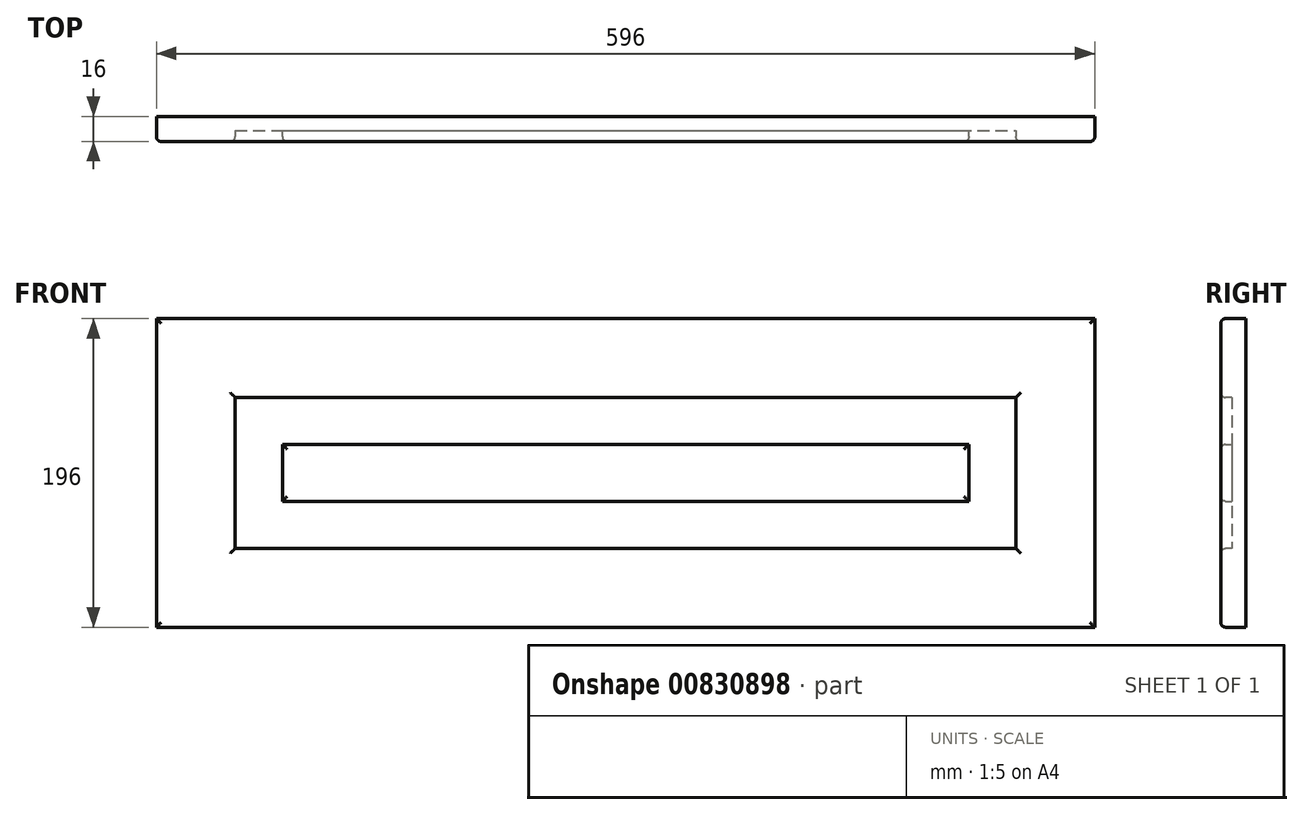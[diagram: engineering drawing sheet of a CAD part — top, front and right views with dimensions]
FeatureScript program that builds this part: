
annotation { "Feature Type Name" : "Feature", "Feature Type Description" : "" }
export const myFeature = defineFeature(function(context is Context, id is Id, definition is map)
    precondition{}
    {
        {
            var Q0;
            Q0=qCreatedBy(makeId("Front.planeOp"),FACE);
            var sketch = newSketch(context, id + "F0", { "sketchPlane" : qUnion([Q0])});
            skLineSegment(sketch, "E0.bottom", {"start": v(0, 0) * mm, "end": v(44.66, 0) * mm});
            skLineSegment(sketch, "E0.top", {"start": v(0, 33.8) * mm, "end": v(44.66, 33.8) * mm});
            skLineSegment(sketch, "E0.left", {"start": v(0, 0) * mm, "end": v(0, 33.8) * mm});
            skLineSegment(sketch, "E0.right", {"start": v(44.66, 0) * mm, "end": v(44.66, 33.8) * mm});
            skSolve(sketch);
        }
        {
            var Q0;
            Q0=makeQuery(id+"F0.imprint","IMPRINT",FACE,{"disambiguationData":[TD([[makeQuery(id+"F0.imprint","IMPRINT",EDGE,{"derivedFrom":sQuery(id+"F0.wireOp",EDGE,"E0.bottom")}),1.0]])]});
            extrude(context, id + "F1", {"entities" : qUnion([Q0]), "depth" : 16 * mm, "offsetDistance" : 25.4 * mm});
        }
        {
            var Q0;
            Q0=makeQuery(id+"F1.opExtrude","SWEPT_FACE",FACE,{"disambiguationData":[OSD([sQuery(id+"F0.wireOp",EDGE,"E0.bottom")])]});
            extrude(context, id + "F2", {"entities" : qUnion([Q0]), "operationType" : NewBodyOperationType.ADD, "oppositeDirection" : true, "depth" : 796 * mm, "offsetDistance" : 25 * mm});
        }
        {
            var Q0;
            {var subQ0=sQuery(id+"F0.wireOp",EDGE,"E0.left");Q0=makeQuery(id+"F2.boolean.opBoolean","MERGE",FACE,{"derivedFrom":[makeQuery(id+"F1.opExtrude","SWEPT_FACE",FACE,{"disambiguationData":[OSD([subQ0])]}),makeQuery(id+"F2.opExtrude","SWEPT_FACE",FACE,{"disambiguationData":[OSD([sQuery(id+"F0.wireOp",EDGE,"E0.bottom"),subQ0])]})]});}
            extrude(context, id + "F3", {"entities" : qUnion([Q0]), "operationType" : NewBodyOperationType.ADD, "oppositeDirection" : true, "depth" : 196 * mm, "offsetDistance" : 25 * mm});
        }
        {
            var Q0;
            {var subQ0=sQuery(id+"F0.wireOp",EDGE,"E0.left");var subQ1=sQuery(id+"F0.wireOp",EDGE,"E0.bottom");Q0=makeQuery(id+"F3.boolean.opBoolean","MERGE",FACE,{"derivedFrom":[makeQuery(id+"F2.boolean.opBoolean","MERGE",FACE,{"derivedFrom":[makeQuery(id+"F1.opExtrude","CAP_FACE",FACE,{"disambiguationData":[OSD([subQ1,sQuery(id+"F0.wireOp",EDGE,"E0.top"),subQ0,sQuery(id+"F0.wireOp",EDGE,"E0.right")])],"isStart":false}),makeQuery(id+"F2.opExtrude","SWEPT_FACE",FACE,{"disambiguationData":[OSD([subQ1]),TDD([makeQuery(id+"F1.opExtrude","CAP_EDGE",EDGE,{"disambiguationData":[OSD([subQ1])],"isStart":false})])]})]}),makeQuery(id+"F3.opExtrude","SWEPT_FACE",FACE,{"disambiguationData":[OSD([subQ1,subQ0]),TDD([makeQuery(id+"F2.boolean.opBoolean","MERGE",EDGE,{"derivedFrom":[makeQuery(id+"F1.opExtrude","CAP_EDGE",EDGE,{"disambiguationData":[OSD([subQ0])],"isStart":false}),makeQuery(id+"F2.opExtrude","SWEPT_EDGE",EDGE,{"disambiguationData":[OSD([subQ1,subQ0]),TDD([makeQuery(id+"F1.opExtrude","CAP_VERTEX",VERTEX,{"disambiguationData":[OSD([subQ1,subQ0])],"isStart":false})])]})]})])]})]});}
            var sketch = newSketch(context, id + "F4", { "sketchPlane" : qUnion([Q0])});
            skLineSegment(sketch, "E1.bottom", {"start": v(59.7, 646.67) * mm, "end": v(128.66, 646.67) * mm});
            skLineSegment(sketch, "E1.top", {"start": v(59.7, 152.97) * mm, "end": v(128.66, 152.97) * mm});
            skLineSegment(sketch, "E1.left", {"start": v(59.7, 646.67) * mm, "end": v(59.7, 152.97) * mm});
            skLineSegment(sketch, "E1.right", {"start": v(128.66, 646.67) * mm, "end": v(128.66, 152.97) * mm});
            skSolve(sketch);
        }
        {
            var Q0;
            Q0=makeQuery(id+"F4.imprint","IMPRINT",FACE,{"disambiguationData":[TD([[makeQuery(id+"F4.imprint","IMPRINT",EDGE,{"derivedFrom":sQuery(id+"F4.wireOp",EDGE,"E1.bottom")}),-1.0]])]});
            extrude(context, id + "F5", {"entities" : qUnion([Q0]), "operationType" : NewBodyOperationType.REMOVE, "oppositeDirection" : true, "depth" : 7 * mm, "offsetDistance" : 25 * mm});
        }
        {
            var Q0;
            Q0=makeQuery(id+"F5.boolean.opBoolean","COPY",FACE,{"derivedFrom":makeQuery(id+"F5.opExtrude","SWEPT_FACE",FACE,{"disambiguationData":[OSD([sQuery(id+"F4.wireOp",EDGE,"E1.left")])]})});
            extrude(context, id + "F6", {"entities" : qUnion([Q0]), "operationType" : NewBodyOperationType.REMOVE, "oppositeDirection" : true, "depth" : 9.7 * mm, "offsetDistance" : 25 * mm});
        }
        {
            var Q0;
            {var subQ0=sQuery(id+"F4.wireOp",EDGE,"E1.bottom");Q0=makeQuery(id+"F6.boolean.opBoolean","MERGE",FACE,{"derivedFrom":[makeQuery(id+"F5.boolean.opBoolean","COPY",FACE,{"derivedFrom":makeQuery(id+"F5.opExtrude","SWEPT_FACE",FACE,{"disambiguationData":[OSD([subQ0])]})}),makeQuery(id+"F6.opExtrude","SWEPT_FACE",FACE,{"disambiguationData":[OSD([subQ0,sQuery(id+"F4.wireOp",EDGE,"E1.left")])]})]});}
            extrude(context, id + "F7", {"entities" : qUnion([Q0]), "operationType" : NewBodyOperationType.ADD, "oppositeDirection" : true, "depth" : 99.33 * mm, "offsetDistance" : 25 * mm});
        }
        {
            var Q0;
            {var subQ0=sQuery(id+"F4.wireOp",EDGE,"E1.bottom");Q0=makeQuery(id+"F6.boolean.opBoolean","MERGE",FACE,{"derivedFrom":[makeQuery(id+"F5.boolean.opBoolean","COPY",FACE,{"derivedFrom":makeQuery(id+"F5.opExtrude","SWEPT_FACE",FACE,{"disambiguationData":[OSD([subQ0])]})}),makeQuery(id+"F6.opExtrude","SWEPT_FACE",FACE,{"disambiguationData":[OSD([subQ0,sQuery(id+"F4.wireOp",EDGE,"E1.left")])]})]});}
            extrude(context, id + "F8", {"entities" : qUnion([Q0]), "operationType" : NewBodyOperationType.REMOVE, "oppositeDirection" : true, "depth" : 99.33 * mm, "offsetDistance" : 25 * mm});
        }
        {
            var Q0;
            {var subQ0=sQuery(id+"F4.wireOp",EDGE,"E1.right");Q0=makeQuery(id+"F8.boolean.opBoolean","MERGE",FACE,{"derivedFrom":[makeQuery(id+"F5.boolean.opBoolean","COPY",FACE,{"derivedFrom":makeQuery(id+"F5.opExtrude","SWEPT_FACE",FACE,{"disambiguationData":[OSD([subQ0])]})}),makeQuery(id+"F8.opExtrude","SWEPT_FACE",FACE,{"disambiguationData":[OSD([sQuery(id+"F4.wireOp",EDGE,"E1.bottom"),subQ0])]})]});}
            extrude(context, id + "F9", {"entities" : qUnion([Q0]), "operationType" : NewBodyOperationType.REMOVE, "oppositeDirection" : true, "depth" : 17.34 * mm, "offsetDistance" : 25 * mm});
        }
        {
            var Q0;
            {var subQ0=sQuery(id+"F4.wireOp",EDGE,"E1.top");Q0=makeQuery(id+"F9.boolean.opBoolean","MERGE",FACE,{"derivedFrom":[makeQuery(id+"F6.boolean.opBoolean","MERGE",FACE,{"derivedFrom":[makeQuery(id+"F5.boolean.opBoolean","COPY",FACE,{"derivedFrom":makeQuery(id+"F5.opExtrude","SWEPT_FACE",FACE,{"disambiguationData":[OSD([subQ0])]})}),makeQuery(id+"F6.opExtrude","SWEPT_FACE",FACE,{"disambiguationData":[OSD([subQ0,sQuery(id+"F4.wireOp",EDGE,"E1.left")])]})]}),makeQuery(id+"F9.opExtrude","SWEPT_FACE",FACE,{"disambiguationData":[OSD([subQ0,sQuery(id+"F4.wireOp",EDGE,"E1.right")])]})]});}
            extrude(context, id + "F10", {"entities" : qUnion([Q0]), "operationType" : NewBodyOperationType.REMOVE, "oppositeDirection" : true, "depth" : 102.97 * mm, "offsetDistance" : 25 * mm});
        }
        {
            var Q0;
            {var subQ0=sQuery(id+"F4.wireOp",EDGE,"E1.right");var subQ1=sQuery(id+"F4.wireOp",EDGE,"E1.top");var subQ2=sQuery(id+"F4.wireOp",EDGE,"E1.left");var subQ3=sQuery(id+"F4.wireOp",EDGE,"E1.bottom");Q0=makeQuery(id+"F10.boolean.opBoolean","MERGE",FACE,{"derivedFrom":[makeQuery(id+"F9.boolean.opBoolean","MERGE",FACE,{"derivedFrom":[makeQuery(id+"F8.boolean.opBoolean","MERGE",FACE,{"derivedFrom":[makeQuery(id+"F6.boolean.opBoolean","MERGE",FACE,{"derivedFrom":[makeQuery(id+"F5.boolean.opBoolean","COPY",FACE,{"derivedFrom":makeQuery(id+"F5.opExtrude","CAP_FACE",FACE,{"disambiguationData":[OSD([subQ3,subQ1,subQ2,subQ0])],"isStart":false})}),makeQuery(id+"F6.opExtrude","SWEPT_FACE",FACE,{"disambiguationData":[OSD([subQ2]),TDD([makeQuery(id+"F5.boolean.opBoolean","COPY",EDGE,{"derivedFrom":makeQuery(id+"F5.opExtrude","CAP_EDGE",EDGE,{"disambiguationData":[OSD([subQ2])],"isStart":false})})])]})]}),makeQuery(id+"F8.opExtrude","SWEPT_FACE",FACE,{"disambiguationData":[OSD([subQ3,subQ2]),TDD([makeQuery(id+"F6.boolean.opBoolean","MERGE",EDGE,{"derivedFrom":[makeQuery(id+"F5.boolean.opBoolean","COPY",EDGE,{"derivedFrom":makeQuery(id+"F5.opExtrude","CAP_EDGE",EDGE,{"disambiguationData":[OSD([subQ3])],"isStart":false})}),makeQuery(id+"F6.opExtrude","SWEPT_EDGE",EDGE,{"disambiguationData":[OSD([subQ3,subQ2]),TDD([makeQuery(id+"F5.boolean.opBoolean","COPY",VERTEX,{"derivedFrom":makeQuery(id+"F5.opExtrude","CAP_VERTEX",VERTEX,{"disambiguationData":[OSD([subQ3,subQ2])],"isStart":false})})])]})]})])]})]}),makeQuery(id+"F9.opExtrude","SWEPT_FACE",FACE,{"disambiguationData":[OSD([subQ3,subQ0]),TDD([makeQuery(id+"F8.boolean.opBoolean","MERGE",EDGE,{"derivedFrom":[makeQuery(id+"F5.boolean.opBoolean","COPY",EDGE,{"derivedFrom":makeQuery(id+"F5.opExtrude","CAP_EDGE",EDGE,{"disambiguationData":[OSD([subQ0])],"isStart":false})}),makeQuery(id+"F8.opExtrude","SWEPT_EDGE",EDGE,{"disambiguationData":[OSD([subQ3,subQ0]),TDD([makeQuery(id+"F5.boolean.opBoolean","COPY",VERTEX,{"derivedFrom":makeQuery(id+"F5.opExtrude","CAP_VERTEX",VERTEX,{"disambiguationData":[OSD([subQ3,subQ0])],"isStart":false})})])]})]})])]})]}),makeQuery(id+"F10.opExtrude","SWEPT_FACE",FACE,{"disambiguationData":[OSD([subQ1,subQ2,subQ0]),TDD([makeQuery(id+"F9.boolean.opBoolean","MERGE",EDGE,{"derivedFrom":[makeQuery(id+"F6.boolean.opBoolean","MERGE",EDGE,{"derivedFrom":[makeQuery(id+"F5.boolean.opBoolean","COPY",EDGE,{"derivedFrom":makeQuery(id+"F5.opExtrude","CAP_EDGE",EDGE,{"disambiguationData":[OSD([subQ1])],"isStart":false})}),makeQuery(id+"F6.opExtrude","SWEPT_EDGE",EDGE,{"disambiguationData":[OSD([subQ1,subQ2]),TDD([makeQuery(id+"F5.boolean.opBoolean","COPY",VERTEX,{"derivedFrom":makeQuery(id+"F5.opExtrude","CAP_VERTEX",VERTEX,{"disambiguationData":[OSD([subQ1,subQ2])],"isStart":false})})])]})]}),makeQuery(id+"F9.opExtrude","SWEPT_EDGE",EDGE,{"disambiguationData":[OSD([subQ1,subQ0]),TDD([makeQuery(id+"F5.boolean.opBoolean","COPY",VERTEX,{"derivedFrom":makeQuery(id+"F5.opExtrude","CAP_VERTEX",VERTEX,{"disambiguationData":[OSD([subQ1,subQ0])],"isStart":false})})])]})]})])]})]});}
            var sketch = newSketch(context, id + "F11", { "sketchPlane" : qUnion([Q0])});
            skLineSegment(sketch, "E2.bottom", {"start": v(74.13, 678.73) * mm, "end": v(109.41, 678.73) * mm});
            skLineSegment(sketch, "E2.top", {"start": v(74.13, 186.63) * mm, "end": v(109.41, 186.63) * mm});
            skLineSegment(sketch, "E2.left", {"start": v(74.13, 678.73) * mm, "end": v(74.13, 186.63) * mm});
            skLineSegment(sketch, "E2.right", {"start": v(109.41, 678.73) * mm, "end": v(109.41, 186.63) * mm});
            skSolve(sketch);
        }
        {
            var Q0;
            Q0=makeQuery(id+"F11.imprint","IMPRINT",FACE,{"disambiguationData":[TD([[makeQuery(id+"F11.imprint","IMPRINT",EDGE,{"derivedFrom":sQuery(id+"F11.wireOp",EDGE,"E2.bottom")}),-1.0]])]});
            extrude(context, id + "F12", {"entities" : qUnion([Q0]), "operationType" : NewBodyOperationType.ADD, "depth" : 7 * mm, "offsetDistance" : 25 * mm});
        }
        {
            var Q0;
            Q0=makeQuery(id+"F12.opExtrude","SWEPT_FACE",FACE,{"disambiguationData":[OSD([sQuery(id+"F11.wireOp",EDGE,"E2.bottom")])]});
            extrude(context, id + "F13", {"entities" : qUnion([Q0]), "operationType" : NewBodyOperationType.ADD, "depth" : 37.27 * mm, "offsetDistance" : 25 * mm});
        }
        {
            var Q0;
            {var subQ0=sQuery(id+"F11.wireOp",EDGE,"E2.right");Q0=makeQuery(id+"F13.boolean.opBoolean","MERGE",FACE,{"derivedFrom":[makeQuery(id+"F12.opExtrude","SWEPT_FACE",FACE,{"disambiguationData":[OSD([subQ0])]}),makeQuery(id+"F13.opExtrude","SWEPT_FACE",FACE,{"disambiguationData":[OSD([sQuery(id+"F11.wireOp",EDGE,"E2.bottom"),subQ0])]})]});}
            extrude(context, id + "F14", {"entities" : qUnion([Q0]), "operationType" : NewBodyOperationType.ADD, "depth" : 6.58 * mm, "offsetDistance" : 25 * mm});
        }
        {
            var Q0;
            {var subQ0=sQuery(id+"F11.wireOp",EDGE,"E2.top");Q0=makeQuery(id+"F14.boolean.opBoolean","MERGE",FACE,{"derivedFrom":[makeQuery(id+"F12.opExtrude","SWEPT_FACE",FACE,{"disambiguationData":[OSD([subQ0])]}),makeQuery(id+"F14.opExtrude","SWEPT_FACE",FACE,{"disambiguationData":[OSD([subQ0,sQuery(id+"F11.wireOp",EDGE,"E2.right")])]})]});}
            extrude(context, id + "F15", {"entities" : qUnion([Q0]), "operationType" : NewBodyOperationType.ADD, "depth" : 106.63 * mm, "offsetDistance" : 25 * mm});
        }
        {
            var Q0;
            {var subQ0=sQuery(id+"F11.wireOp",EDGE,"E2.left");Q0=makeQuery(id+"F15.boolean.opBoolean","MERGE",FACE,{"derivedFrom":[makeQuery(id+"F13.boolean.opBoolean","MERGE",FACE,{"derivedFrom":[makeQuery(id+"F12.opExtrude","SWEPT_FACE",FACE,{"disambiguationData":[OSD([subQ0])]}),makeQuery(id+"F13.opExtrude","SWEPT_FACE",FACE,{"disambiguationData":[OSD([sQuery(id+"F11.wireOp",EDGE,"E2.bottom"),subQ0])]})]}),makeQuery(id+"F15.opExtrude","SWEPT_FACE",FACE,{"disambiguationData":[OSD([sQuery(id+"F11.wireOp",EDGE,"E2.top"),subQ0])]})]});}
            extrude(context, id + "F16", {"entities" : qUnion([Q0]), "operationType" : NewBodyOperationType.REMOVE, "oppositeDirection" : true, "depth" : 5.87 * mm, "offsetDistance" : 25 * mm});
        }
        {
            var Q0;
            Q0=makeQuery(id+"F3.opExtrude","CAP_FACE",FACE,{"disambiguationData":[OSD([sQuery(id+"F0.wireOp",EDGE,"E0.bottom"),sQuery(id+"F0.wireOp",EDGE,"E0.left")])],"isStart":false});
            extrude(context, id + "F17", {"entities" : qUnion([Q0]), "operationType" : NewBodyOperationType.ADD, "depth" : 200 * mm, "offsetDistance" : 25 * mm});
        }
        {
            var Q0;
            {var subQ0=sQuery(id+"F4.wireOp",EDGE,"E1.right");Q0=makeQuery(id+"F10.boolean.opBoolean","MERGE",FACE,{"derivedFrom":[makeQuery(id+"F9.boolean.opBoolean","COPY",FACE,{"derivedFrom":makeQuery(id+"F9.opExtrude","CAP_FACE",FACE,{"disambiguationData":[OSD([sQuery(id+"F4.wireOp",EDGE,"E1.bottom"),subQ0])],"isStart":false})}),makeQuery(id+"F10.opExtrude","SWEPT_FACE",FACE,{"disambiguationData":[OSD([sQuery(id+"F4.wireOp",EDGE,"E1.top"),subQ0])]})]});}
            extrude(context, id + "F18", {"entities" : qUnion([Q0]), "operationType" : NewBodyOperationType.REMOVE, "oppositeDirection" : true, "depth" : 200 * mm, "offsetDistance" : 25 * mm});
        }
        {
            var Q0;
            {var subQ0=sQuery(id+"F11.wireOp",EDGE,"E2.right");var subQ1=sQuery(id+"F11.wireOp",EDGE,"E2.top");Q0=makeQuery(id+"F15.boolean.opBoolean","MERGE",FACE,{"derivedFrom":[makeQuery(id+"F14.opExtrude","CAP_FACE",FACE,{"disambiguationData":[OSD([sQuery(id+"F11.wireOp",EDGE,"E2.bottom"),subQ0])],"isStart":false}),makeQuery(id+"F15.opExtrude","SWEPT_FACE",FACE,{"disambiguationData":[OSD([subQ1,subQ0]),TDD([makeQuery(id+"F14.opExtrude","CAP_EDGE",EDGE,{"disambiguationData":[OSD([subQ1,subQ0])],"isStart":false})])]})]});}
            extrude(context, id + "F19", {"entities" : qUnion([Q0]), "operationType" : NewBodyOperationType.ADD, "depth" : 200 * mm, "offsetDistance" : 25 * mm});
        }
        {
            var Q0;
            Q0=makeQuery(id+"F17.opExtrude","CAP_FACE",FACE,{"disambiguationData":[OSD([sQuery(id+"F0.wireOp",EDGE,"E0.bottom"),sQuery(id+"F0.wireOp",EDGE,"E0.left")])],"isStart":false});
            extrude(context, id + "F20", {"entities" : qUnion([Q0]), "operationType" : NewBodyOperationType.ADD, "depth" : 200 * mm, "offsetDistance" : 25 * mm});
        }
        {
            var Q0;
            Q0=makeQuery(id+"F18.boolean.opBoolean","COPY",FACE,{"derivedFrom":makeQuery(id+"F18.opExtrude","CAP_FACE",FACE,{"disambiguationData":[OSD([sQuery(id+"F4.wireOp",EDGE,"E1.bottom"),sQuery(id+"F4.wireOp",EDGE,"E1.top"),sQuery(id+"F4.wireOp",EDGE,"E1.right")])],"isStart":false})});
            extrude(context, id + "F21", {"entities" : qUnion([Q0]), "operationType" : NewBodyOperationType.REMOVE, "oppositeDirection" : true, "depth" : 200 * mm, "offsetDistance" : 25 * mm});
        }
        {
            var Q0;
            Q0=makeQuery(id+"F19.opExtrude","CAP_FACE",FACE,{"disambiguationData":[OSD([sQuery(id+"F11.wireOp",EDGE,"E2.bottom"),sQuery(id+"F11.wireOp",EDGE,"E2.top"),sQuery(id+"F11.wireOp",EDGE,"E2.right")])],"isStart":false});
            extrude(context, id + "F22", {"entities" : qUnion([Q0]), "operationType" : NewBodyOperationType.ADD, "depth" : 200 * mm, "offsetDistance" : 25 * mm});
        }
        {
            var Q0;
            {var subQ0=sQuery(id+"F11.wireOp",EDGE,"E2.right");var subQ1=sQuery(id+"F11.wireOp",EDGE,"E2.top");Q0=makeQuery(id+"F22.boolean.opBoolean","MERGE",FACE,{"derivedFrom":[makeQuery(id+"F19.boolean.opBoolean","MERGE",FACE,{"derivedFrom":[makeQuery(id+"F15.opExtrude","CAP_FACE",FACE,{"disambiguationData":[OSD([subQ1,subQ0])],"isStart":false}),makeQuery(id+"F19.opExtrude","SWEPT_FACE",FACE,{"disambiguationData":[OSD([subQ1,subQ0])]})]}),makeQuery(id+"F22.opExtrude","SWEPT_FACE",FACE,{"disambiguationData":[OSD([subQ1,subQ0])]})]});}
            extrude(context, id + "F23", {"entities" : qUnion([Q0]), "operationType" : NewBodyOperationType.REMOVE, "oppositeDirection" : true, "depth" : 600 * mm, "offsetDistance" : 25 * mm});
        }
        {
            var Q0;
            {var subQ0=sQuery(id+"F4.wireOp",EDGE,"E1.right");var subQ1=sQuery(id+"F4.wireOp",EDGE,"E1.top");Q0=makeQuery(id+"F21.boolean.opBoolean","MERGE",FACE,{"derivedFrom":[makeQuery(id+"F18.boolean.opBoolean","MERGE",FACE,{"derivedFrom":[makeQuery(id+"F10.boolean.opBoolean","COPY",FACE,{"derivedFrom":makeQuery(id+"F10.opExtrude","CAP_FACE",FACE,{"disambiguationData":[OSD([subQ1,sQuery(id+"F4.wireOp",EDGE,"E1.left"),subQ0])],"isStart":false})}),makeQuery(id+"F18.opExtrude","SWEPT_FACE",FACE,{"disambiguationData":[OSD([subQ1,subQ0])]})]}),makeQuery(id+"F21.opExtrude","SWEPT_FACE",FACE,{"disambiguationData":[OSD([subQ1,subQ0])]})]});}
            extrude(context, id + "F24", {"entities" : qUnion([Q0]), "operationType" : NewBodyOperationType.ADD, "depth" : 600 * mm, "offsetDistance" : 25 * mm});
        }
        {
            var Q0;
            {var subQ0=sQuery(id+"F0.wireOp",EDGE,"E0.left");var subQ1=sQuery(id+"F0.wireOp",EDGE,"E0.bottom");var subQ2=makeQuery(id+"F1.opExtrude","SWEPT_EDGE",EDGE,{"disambiguationData":[OSD([subQ1,subQ0])]});var subQ3=makeQuery(id+"F3.opExtrude","CAP_EDGE",EDGE,{"disambiguationData":[OSD([subQ1,subQ0]),TDD([subQ2])],"isStart":false});Q0=makeQuery(id+"F20.boolean.opBoolean","MERGE",FACE,{"derivedFrom":[makeQuery(id+"F17.boolean.opBoolean","MERGE",FACE,{"derivedFrom":[makeQuery(id+"F3.boolean.opBoolean","MERGE",FACE,{"derivedFrom":[makeQuery(id+"F1.opExtrude","SWEPT_FACE",FACE,{"disambiguationData":[OSD([subQ1])]}),makeQuery(id+"F3.opExtrude","SWEPT_FACE",FACE,{"disambiguationData":[OSD([subQ1,subQ0]),TDD([subQ2])]})]}),makeQuery(id+"F17.opExtrude","SWEPT_FACE",FACE,{"disambiguationData":[OSD([subQ1,subQ0]),TDD([subQ3])]})]}),makeQuery(id+"F20.opExtrude","SWEPT_FACE",FACE,{"disambiguationData":[OSD([subQ1,subQ0]),TDD([makeQuery(id+"F17.opExtrude","CAP_EDGE",EDGE,{"disambiguationData":[OSD([subQ1,subQ0]),TDD([subQ3])],"isStart":false})])]})]});}
            extrude(context, id + "F25", {"entities" : qUnion([Q0]), "operationType" : NewBodyOperationType.REMOVE, "oppositeDirection" : true, "depth" : 600 * mm, "offsetDistance" : 25 * mm});
        }
        {
            var Q0;
            {var subQ0=sQuery(id+"F4.wireOp",EDGE,"E1.right");var subQ1=sQuery(id+"F4.wireOp",EDGE,"E1.top");var subQ2=makeQuery(id+"F5.boolean.opBoolean","COPY",VERTEX,{"derivedFrom":makeQuery(id+"F5.opExtrude","CAP_VERTEX",VERTEX,{"disambiguationData":[OSD([subQ1,subQ0])],"isStart":true})});var subQ3=makeQuery(id+"F10.boolean.opBoolean","COPY",VERTEX,{"derivedFrom":makeQuery(id+"F10.opExtrude","CAP_VERTEX",VERTEX,{"disambiguationData":[OSD([subQ1,subQ0]),TDD([makeQuery(id+"F9.boolean.opBoolean","COPY",VERTEX,{"derivedFrom":makeQuery(id+"F9.opExtrude","CAP_VERTEX",VERTEX,{"disambiguationData":[OSD([subQ1,subQ0]),TDD([subQ2])],"isStart":false})})])],"isStart":false})});var subQ4=sQuery(id+"F4.wireOp",EDGE,"E1.left");var subQ5=sQuery(id+"F0.wireOp",EDGE,"E0.left");var subQ6=sQuery(id+"F0.wireOp",EDGE,"E0.bottom");var subQ7=makeQuery(id+"F2.boolean.opBoolean","MERGE",EDGE,{"derivedFrom":[makeQuery(id+"F1.opExtrude","CAP_EDGE",EDGE,{"disambiguationData":[OSD([subQ5])],"isStart":false}),makeQuery(id+"F2.opExtrude","SWEPT_EDGE",EDGE,{"disambiguationData":[OSD([subQ6,subQ5]),TDD([makeQuery(id+"F1.opExtrude","CAP_VERTEX",VERTEX,{"disambiguationData":[OSD([subQ6,subQ5])],"isStart":false})])]})]});var subQ8=makeQuery(id+"F3.opExtrude","CAP_EDGE",EDGE,{"disambiguationData":[OSD([subQ6,subQ5]),TDD([subQ7])],"isStart":false});Q0=makeQuery(id+"F24.boolean.opBoolean","MERGE",FACE,{"derivedFrom":[makeQuery(id+"F20.boolean.opBoolean","MERGE",FACE,{"derivedFrom":[makeQuery(id+"F17.boolean.opBoolean","MERGE",FACE,{"derivedFrom":[makeQuery(id+"F3.boolean.opBoolean","MERGE",FACE,{"derivedFrom":[makeQuery(id+"F2.boolean.opBoolean","MERGE",FACE,{"derivedFrom":[makeQuery(id+"F1.opExtrude","CAP_FACE",FACE,{"disambiguationData":[OSD([subQ6,sQuery(id+"F0.wireOp",EDGE,"E0.top"),subQ5,sQuery(id+"F0.wireOp",EDGE,"E0.right")])],"isStart":false}),makeQuery(id+"F2.opExtrude","SWEPT_FACE",FACE,{"disambiguationData":[OSD([subQ6]),TDD([makeQuery(id+"F1.opExtrude","CAP_EDGE",EDGE,{"disambiguationData":[OSD([subQ6])],"isStart":false})])]})]}),makeQuery(id+"F3.opExtrude","SWEPT_FACE",FACE,{"disambiguationData":[OSD([subQ6,subQ5]),TDD([subQ7])]})]}),makeQuery(id+"F17.opExtrude","SWEPT_FACE",FACE,{"disambiguationData":[OSD([subQ6,subQ5]),TDD([subQ8])]})]}),makeQuery(id+"F20.opExtrude","SWEPT_FACE",FACE,{"disambiguationData":[OSD([subQ6,subQ5]),TDD([makeQuery(id+"F17.opExtrude","CAP_EDGE",EDGE,{"disambiguationData":[OSD([subQ6,subQ5]),TDD([subQ8])],"isStart":false})])]})]}),makeQuery(id+"F24.opExtrude","SWEPT_FACE",FACE,{"disambiguationData":[OSD([subQ1,subQ4,subQ0]),TDD([makeQuery(id+"F21.boolean.opBoolean","MERGE",EDGE,{"derivedFrom":[makeQuery(id+"F18.boolean.opBoolean","MERGE",EDGE,{"derivedFrom":[makeQuery(id+"F10.boolean.opBoolean","COPY",EDGE,{"derivedFrom":makeQuery(id+"F10.opExtrude","CAP_EDGE",EDGE,{"disambiguationData":[OSD([subQ1,subQ4,subQ0]),TDD([makeQuery(id+"F9.boolean.opBoolean","MERGE",EDGE,{"derivedFrom":[makeQuery(id+"F6.boolean.opBoolean","MERGE",EDGE,{"derivedFrom":[makeQuery(id+"F5.boolean.opBoolean","COPY",EDGE,{"derivedFrom":makeQuery(id+"F5.opExtrude","CAP_EDGE",EDGE,{"disambiguationData":[OSD([subQ1])],"isStart":true})}),makeQuery(id+"F6.opExtrude","SWEPT_EDGE",EDGE,{"disambiguationData":[OSD([subQ1,subQ4]),TDD([makeQuery(id+"F5.boolean.opBoolean","COPY",VERTEX,{"derivedFrom":makeQuery(id+"F5.opExtrude","CAP_VERTEX",VERTEX,{"disambiguationData":[OSD([subQ1,subQ4])],"isStart":true})})])]})]}),makeQuery(id+"F9.opExtrude","SWEPT_EDGE",EDGE,{"disambiguationData":[OSD([subQ1,subQ0]),TDD([subQ2])]})]})])],"isStart":false})}),makeQuery(id+"F18.opExtrude","SWEPT_EDGE",EDGE,{"disambiguationData":[OSD([subQ1,subQ0]),TDD([subQ3])]})]}),makeQuery(id+"F21.opExtrude","SWEPT_EDGE",EDGE,{"disambiguationData":[OSD([subQ1,subQ0]),TDD([makeQuery(id+"F18.boolean.opBoolean","COPY",VERTEX,{"derivedFrom":makeQuery(id+"F18.opExtrude","CAP_VERTEX",VERTEX,{"disambiguationData":[OSD([subQ1,subQ0]),TDD([subQ3])],"isStart":false})})])]})]})])]})]});}
            var Q1;
            {var subQ0=sQuery(id+"F11.wireOp",EDGE,"E2.right");var subQ1=sQuery(id+"F11.wireOp",EDGE,"E2.top");var subQ2=makeQuery(id+"F12.opExtrude","CAP_VERTEX",VERTEX,{"disambiguationData":[OSD([subQ1,subQ0])],"isStart":false});var subQ3=sQuery(id+"F11.wireOp",EDGE,"E2.bottom");var subQ4=makeQuery(id+"F13.boolean.opBoolean","MERGE",EDGE,{"derivedFrom":[makeQuery(id+"F12.opExtrude","CAP_EDGE",EDGE,{"disambiguationData":[OSD([subQ0])],"isStart":false}),makeQuery(id+"F13.opExtrude","SWEPT_EDGE",EDGE,{"disambiguationData":[OSD([subQ3,subQ0]),TDD([makeQuery(id+"F12.opExtrude","CAP_VERTEX",VERTEX,{"disambiguationData":[OSD([subQ3,subQ0])],"isStart":false})])]})]});var subQ5=makeQuery(id+"F15.boolean.opBoolean","MERGE",EDGE,{"derivedFrom":[makeQuery(id+"F14.opExtrude","CAP_EDGE",EDGE,{"disambiguationData":[OSD([subQ3,subQ0]),TDD([subQ4])],"isStart":false}),makeQuery(id+"F15.opExtrude","SWEPT_EDGE",EDGE,{"disambiguationData":[OSD([subQ1,subQ0]),TDD([makeQuery(id+"F14.opExtrude","CAP_VERTEX",VERTEX,{"disambiguationData":[OSD([subQ1,subQ0]),TDD([subQ2])],"isStart":false})])]})]});Q1=makeQuery(id+"F22.boolean.opBoolean","MERGE",FACE,{"derivedFrom":[makeQuery(id+"F19.boolean.opBoolean","MERGE",FACE,{"derivedFrom":[makeQuery(id+"F15.boolean.opBoolean","MERGE",FACE,{"derivedFrom":[makeQuery(id+"F14.boolean.opBoolean","MERGE",FACE,{"derivedFrom":[makeQuery(id+"F13.boolean.opBoolean","MERGE",FACE,{"derivedFrom":[makeQuery(id+"F12.opExtrude","CAP_FACE",FACE,{"disambiguationData":[OSD([subQ3,subQ1,sQuery(id+"F11.wireOp",EDGE,"E2.left"),subQ0])],"isStart":false}),makeQuery(id+"F13.opExtrude","SWEPT_FACE",FACE,{"disambiguationData":[OSD([subQ3]),TDD([makeQuery(id+"F12.opExtrude","CAP_EDGE",EDGE,{"disambiguationData":[OSD([subQ3])],"isStart":false})])]})]}),makeQuery(id+"F14.opExtrude","SWEPT_FACE",FACE,{"disambiguationData":[OSD([subQ3,subQ0]),TDD([subQ4])]})]}),makeQuery(id+"F15.opExtrude","SWEPT_FACE",FACE,{"disambiguationData":[OSD([subQ1,subQ0]),TDD([makeQuery(id+"F14.boolean.opBoolean","MERGE",EDGE,{"derivedFrom":[makeQuery(id+"F12.opExtrude","CAP_EDGE",EDGE,{"disambiguationData":[OSD([subQ1])],"isStart":false}),makeQuery(id+"F14.opExtrude","SWEPT_EDGE",EDGE,{"disambiguationData":[OSD([subQ1,subQ0]),TDD([subQ2])]})]})])]})]}),makeQuery(id+"F19.opExtrude","SWEPT_FACE",FACE,{"disambiguationData":[OSD([subQ3,subQ1,subQ0]),TDD([subQ5])]})]}),makeQuery(id+"F22.opExtrude","SWEPT_FACE",FACE,{"disambiguationData":[OSD([subQ3,subQ1,subQ0]),TDD([makeQuery(id+"F19.opExtrude","CAP_EDGE",EDGE,{"disambiguationData":[OSD([subQ3,subQ1,subQ0]),TDD([subQ5])],"isStart":false})])]})]});}
            fillet(context, id + "F26", {"entities" : qUnion([Q0, Q1]), "radius" : 3 * mm, "tangentPropagation" : true, "allowEdgeOverflow" : false});
        }
    });
